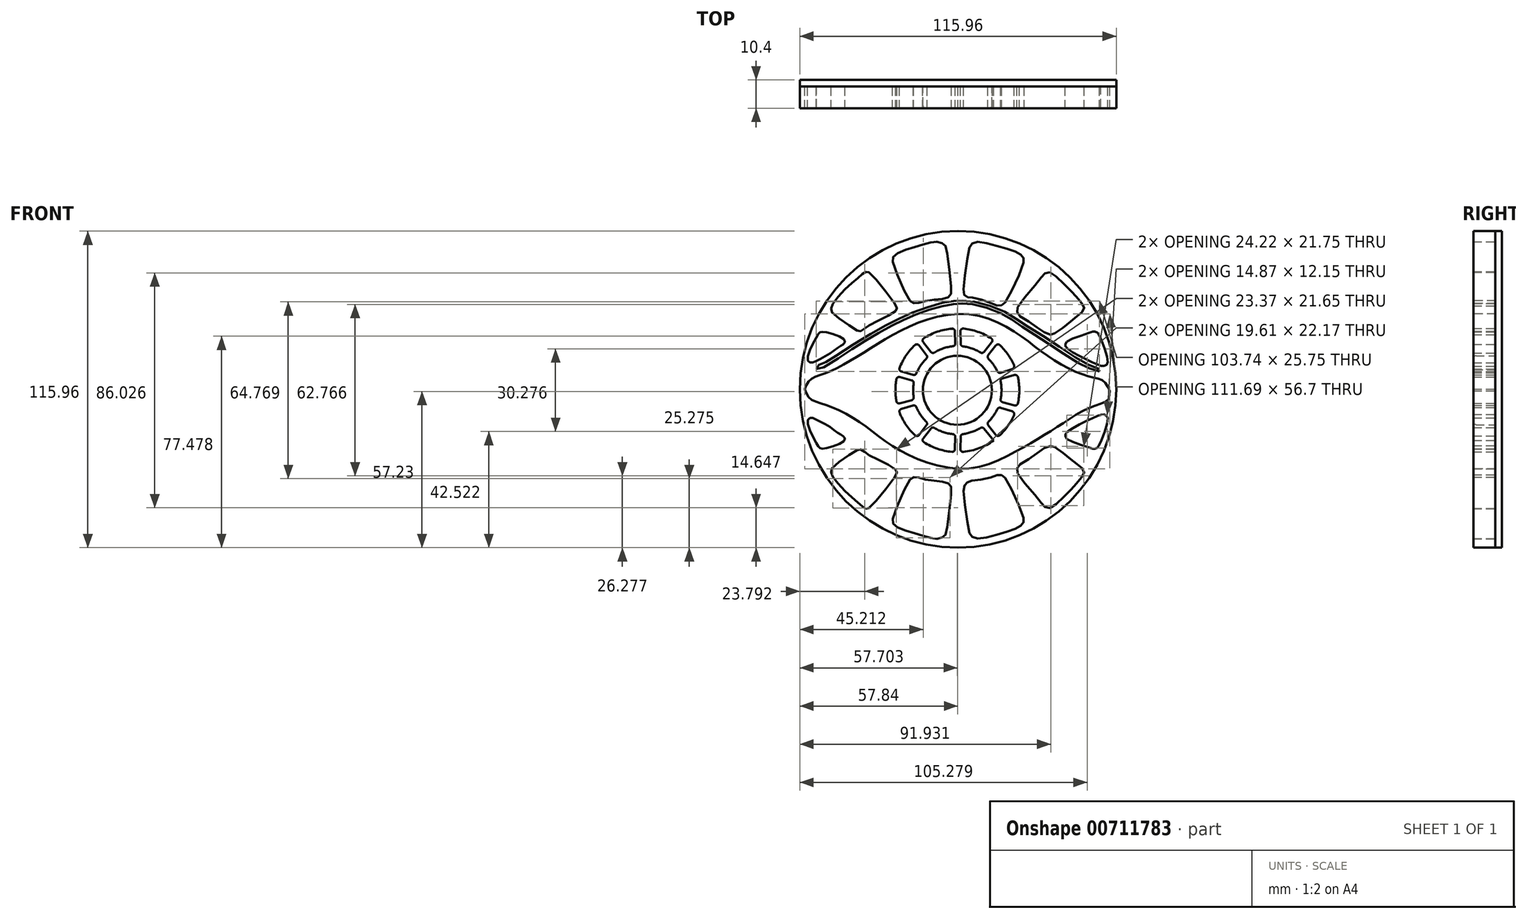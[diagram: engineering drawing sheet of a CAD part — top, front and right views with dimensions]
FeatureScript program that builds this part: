
annotation { "Feature Type Name" : "Feature", "Feature Type Description" : "" }
export const myFeature = defineFeature(function(context is Context, id is Id, definition is map)
    precondition{}
    {
        {
            var Q0;
            Q0=qCreatedBy(makeId("Front.planeOp"),FACE);
            var sketch = newSketch(context, id + "F0", { "sketchPlane" : qUnion([Q0])});
            skPoint(sketch, "E0.first.point", {"position": v(-56.19, 0) * mm});
            skPoint(sketch, "E0.second.point", {"position": v(55.8, -3.23) * mm});
            skPoint(sketch, "E0.third.point", {"position": v(-2.74, 55.09) * mm});
            skCircle(sketch, "E1", {"center": v(-0.25, -2.32) * mm, "radius": 12.63 * mm});
            skPoint(sketch, "E1.first.point", {"position": v(-12.67, 0) * mm});
            skPoint(sketch, "E1.second.point", {"position": v(12.27, -3.96) * mm});
            skPoint(sketch, "E1.third.point", {"position": v(2.35, 10.04) * mm});
            skFitSpline(sketch, "E2", {"points": [v(0, 25.6) * mm, v(22.08, 18.16) * mm, v(35.62, 8.4) * mm, v(48.16, 2.67) * mm, v(53.12, 1.17) * mm, v(55.8, -3.23) * mm], "startDerivative": vector(97.64, 3.3) * mm, "endDerivative": vector(12.94, -38.95) * mm});
            skFitSpline(sketch, "E3.MirrorCS", {"points": [v(0, 25.6) * mm, v(-22.75, 18.54) * mm, v(-38.1, 9.34) * mm, v(-48.7, 3.85) * mm, v(-54.13, 1.57) * mm, v(-56.3, -2.43) * mm], "startDerivative": vector(-92.15, -2.88) * mm, "endDerivative": vector(-12.94, -38.95) * mm});
            skFitSpline(sketch, "E4.MirrorCS", {"points": [v(0, -31.1) * mm, v(23.23, -23.62) * mm, v(36.64, -15.57) * mm, v(48.14, -8.8) * mm, v(55.17, -5.48) * mm, v(55.8, -1.41) * mm], "startDerivative": vector(97.64, -3.3) * mm, "endDerivative": vector(12.94, 38.95) * mm});
            skFitSpline(sketch, "E5.MirrorCS", {"points": [v(0, -31.1) * mm, v(-23.18, -23.24) * mm, v(-36.31, -13.78) * mm, v(-48.45, -7.65) * mm, v(-54.13, -5.41) * mm, v(-56.3, -1.41) * mm], "startDerivative": vector(-89.64, 6.19) * mm, "endDerivative": vector(-12.94, 38.95) * mm});
            skFitSpline(sketch, "E6", {"points": [v(-52, 5.4) * mm, v(-45.96, 7.88) * mm, v(-34.5, 15.43) * mm, v(-23.54, 21.65) * mm, v(-15.7, 25.25) * mm, v(-4.7, 28.68) * mm, v(0.44, 29.22) * mm], "startDerivative": vector(38.04, 9.99) * mm, "endDerivative": vector(34.79, 0.33) * mm});
            skFitSpline(sketch, "E7.MirrorCS", {"points": [v(51.82, 4.54) * mm, v(45.93, 6.75) * mm, v(33.9, 14.77) * mm, v(22.85, 21.49) * mm, v(15.76, 25.71) * mm, v(4.84, 29.15) * mm, v(-0.2, 29.2) * mm], "startDerivative": vector(-38.04, 9.99) * mm, "endDerivative": vector(-34.83, 0.37) * mm});
            skFitSpline(sketch, "E8", {"points": [v(-52.01, 8.4) * mm, v(-46.87, 11.2) * mm, v(-43.44, 13.7) * mm, v(-41.72, 14.8) * mm, v(-41.72, 16.2) * mm, v(-48.74, 19) * mm, v(-50.6, 18.84) * mm, v(-51.7, 17.29) * mm, v(-55.1, 9.31) * mm, v(-54.04, 7.78) * mm, v(-52.01, 8.4) * mm]});
            skFitSpline(sketch, "E9", {"points": [v(-45.87, 29.35) * mm, v(-40.77, 35.19) * mm, v(-36.51, 38.99) * mm, v(-34.47, 40.65) * mm, v(-33.45, 41.12) * mm, v(-32.25, 40.56) * mm, v(-22.8, 28.88) * mm, v(-22.42, 27.59) * mm, v(-23.26, 26.38) * mm, v(-31.7, 21.93) * mm, v(-34.29, 20.17) * mm, v(-35.96, 19.25) * mm, v(-37.62, 19.99) * mm, v(-45.96, 25.92) * mm, v(-46.52, 27.4) * mm, v(-45.87, 29.35) * mm]});
            skFitSpline(sketch, "E10", {"points": [v(-22.16, 47.89) * mm, v(-16.65, 49.92) * mm, v(-11.8, 51.3) * mm, v(-8.4, 52.08) * mm, v(-6.5, 51.82) * mm, v(-4.85, 50.9) * mm, v(-4.26, 49.4) * mm, v(-2.5, 34.19) * mm, v(-2.82, 32.55) * mm, v(-3.94, 31.57) * mm, v(-7.28, 30.98) * mm, v(-12.46, 30.26) * mm, v(-15.08, 29.54) * mm, v(-16.52, 29.6) * mm, v(-17.83, 30.72) * mm, v(-23.93, 44.67) * mm, v(-23.8, 46.44) * mm, v(-22.16, 47.89) * mm]});
            skFitSpline(sketch, "E11", {"points": [v(7.16, 52.01) * mm, v(14.24, 50.57) * mm, v(20.86, 48.54) * mm, v(23.28, 47.1) * mm, v(24, 46.05) * mm, v(24.07, 44.54) * mm, v(17.38, 30) * mm, v(16.07, 28.88) * mm, v(14.76, 28.62) * mm, v(11.75, 29.73) * mm, v(5.3, 31.6) * mm, v(3.6, 31.77) * mm, v(2.44, 32.42) * mm, v(2.05, 34.19) * mm, v(4.01, 49.2) * mm, v(5, 51.3) * mm, v(7.16, 52.01) * mm]});
            skFitSpline(sketch, "E12", {"points": [v(21.84, 28.1) * mm, v(29.38, 37.4) * mm, v(31.34, 40.02) * mm, v(32.78, 40.87) * mm, v(34.42, 40.48) * mm, v(39.47, 35.96) * mm, v(42.94, 32.35) * mm, v(45.37, 29.4) * mm, v(46.22, 27.83) * mm, v(45.56, 26.32) * mm, v(43.27, 24.55) * mm, v(39.53, 21.47) * mm, v(34.88, 18.2) * mm, v(33.96, 18.06) * mm, v(31.34, 19.05) * mm, v(26.69, 22.4) * mm, v(21.97, 25.4) * mm, v(21.64, 26.32) * mm, v(21.84, 28.1) * mm]});
            skFitSpline(sketch, "E13", {"points": [v(39.86, 15.5) * mm, v(48.7, 18.92) * mm, v(49.82, 19.24) * mm, v(50.87, 18.85) * mm, v(51.6, 18.13) * mm, v(54.84, 8.73) * mm, v(54.41, 6.99) * mm, v(53.17, 6.53) * mm, v(51.4, 6.99) * mm, v(44.78, 10.07) * mm, v(39.47, 13.54) * mm, v(39.27, 14.33) * mm, v(39.86, 15.5) * mm]});
            skFitSpline(sketch, "E14.MirrorC", {"points": [v(39.86, -20.15) * mm, v(48.7, -23.56) * mm, v(49.82, -23.88) * mm, v(50.87, -23.5) * mm, v(51.6, -22.77) * mm, v(54.84, -13.37) * mm, v(54.41, -11.63) * mm, v(53.17, -11.17) * mm, v(51.4, -11.63) * mm, v(44.78, -14.7) * mm, v(39.47, -18.18) * mm, v(39.27, -18.97) * mm, v(39.86, -20.15) * mm]});
            skFitSpline(sketch, "E15.MirrorC", {"points": [v(21.84, -32.73) * mm, v(29.38, -42.04) * mm, v(31.34, -44.66) * mm, v(32.78, -45.51) * mm, v(34.42, -45.12) * mm, v(39.47, -40.6) * mm, v(42.94, -37) * mm, v(45.37, -34.04) * mm, v(46.22, -32.47) * mm, v(45.56, -30.96) * mm, v(43.27, -29.2) * mm, v(39.53, -26.11) * mm, v(34.88, -22.84) * mm, v(33.96, -22.7) * mm, v(31.34, -23.69) * mm, v(26.69, -27.03) * mm, v(21.97, -30.04) * mm, v(21.64, -30.96) * mm, v(21.84, -32.73) * mm]});
            skFitSpline(sketch, "E16.MirrorC", {"points": [v(7.16, -56.65) * mm, v(14.24, -55.21) * mm, v(20.86, -53.18) * mm, v(23.28, -51.74) * mm, v(24, -50.69) * mm, v(24.07, -49.18) * mm, v(17.38, -34.63) * mm, v(16.07, -33.52) * mm, v(14.76, -33.26) * mm, v(11.75, -34.37) * mm, v(5.06, -35.48) * mm, v(3.5, -36) * mm, v(2.44, -37.06) * mm, v(2.05, -38.83) * mm, v(4.01, -53.83) * mm, v(5, -55.93) * mm, v(7.16, -56.65) * mm]});
            skFitSpline(sketch, "E17.MirrorC", {"points": [v(-22.16, -52.53) * mm, v(-16.65, -54.56) * mm, v(-11.8, -55.93) * mm, v(-8.4, -56.72) * mm, v(-6.5, -56.46) * mm, v(-4.85, -55.54) * mm, v(-4.26, -54.03) * mm, v(-2.5, -38.83) * mm, v(-2.82, -37.19) * mm, v(-3.94, -36.2) * mm, v(-7.28, -35.62) * mm, v(-12.46, -34.9) * mm, v(-15.08, -34.18) * mm, v(-16.52, -34.24) * mm, v(-17.83, -35.35) * mm, v(-23.93, -49.31) * mm, v(-23.8, -51.08) * mm, v(-22.16, -52.53) * mm]});
            skFitSpline(sketch, "E18.MirrorC", {"points": [v(-45.87, -33.99) * mm, v(-40.77, -39.83) * mm, v(-36.51, -43.63) * mm, v(-34.47, -45.3) * mm, v(-33.45, -45.76) * mm, v(-32.25, -45.2) * mm, v(-22.8, -33.52) * mm, v(-22.42, -32.23) * mm, v(-23.26, -31.02) * mm, v(-31.7, -26.57) * mm, v(-34.29, -24.81) * mm, v(-35.96, -23.89) * mm, v(-37.62, -24.63) * mm, v(-45.96, -30.56) * mm, v(-46.52, -32.04) * mm, v(-45.87, -33.99) * mm]});
            skFitSpline(sketch, "E19.MirrorC", {"points": [v(-52.01, -13.04) * mm, v(-46.87, -15.85) * mm, v(-43.44, -18.34) * mm, v(-41.72, -19.43) * mm, v(-41.72, -20.83) * mm, v(-48.74, -23.64) * mm, v(-50.6, -23.48) * mm, v(-51.7, -21.93) * mm, v(-55.1, -13.95) * mm, v(-54.04, -12.42) * mm, v(-52.01, -13.04) * mm]});
            skCircle(sketch, "E20", {"center": v(-0.25, -2.32) * mm, "radius": 58.34 * mm});
            skLineSegment(sketch, "E21.0", {"start": v(-9.43, 11) * mm, "end": v(-13.4, 16.13) * mm});
            skLineSegment(sketch, "E22.0", {"start": v(-10.98, 9.8) * mm, "end": v(-14.95, 14.97) * mm});
            skLineSegment(sketch, "E23.0", {"start": v(0.96, 13.83) * mm, "end": v(0.85, 20.35) * mm});
            skLineSegment(sketch, "E24.0", {"start": v(-0.95, 13.84) * mm, "end": v(-1.17, 20.31) * mm});
            skLineSegment(sketch, "E25.0", {"start": v(-15.55, 3.05) * mm, "end": v(-21.8, 4.82) * mm});
            skLineSegment(sketch, "E26.0", {"start": v(-16.08, 1.06) * mm, "end": v(-22.35, 2.79) * mm});
            skLineSegment(sketch, "E27.0", {"start": v(10.52, 9.8) * mm, "end": v(14.52, 14.93) * mm});
            skLineSegment(sketch, "E28.0", {"start": v(8.94, 11.01) * mm, "end": v(13.03, 16.08) * mm});
            skLineSegment(sketch, "E29.0", {"start": v(15.4, 1.82) * mm, "end": v(21.68, 3.5) * mm});
            skLineSegment(sketch, "E30.0", {"start": v(14.75, 3.82) * mm, "end": v(20.93, 5.8) * mm});
            skPoint(sketch, "E31.MirrorP", {"position": v(2.35, -14.68) * mm});
            skLineSegment(sketch, "E32.MirrorCS", {"start": v(10.52, -14.43) * mm, "end": v(14.52, -19.57) * mm});
            skLineSegment(sketch, "E33.MirrorCS", {"start": v(8.94, -15.65) * mm, "end": v(13.03, -20.72) * mm});
            skLineSegment(sketch, "E34.MirrorCS", {"start": v(-10.98, -14.44) * mm, "end": v(-14.95, -19.61) * mm});
            skLineSegment(sketch, "E35.MirrorCS", {"start": v(-9.43, -15.64) * mm, "end": v(-13.4, -20.77) * mm});
            skLineSegment(sketch, "E36.MirrorCS", {"start": v(-15.55, -7.7) * mm, "end": v(-21.8, -9.46) * mm});
            skLineSegment(sketch, "E37.MirrorCS", {"start": v(0.96, -18.47) * mm, "end": v(0.85, -24.99) * mm});
            skLineSegment(sketch, "E38.MirrorCS", {"start": v(-0.95, -18.48) * mm, "end": v(-1.17, -24.95) * mm});
            skLineSegment(sketch, "E39.MirrorCS", {"start": v(-16.08, -5.7) * mm, "end": v(-22.35, -7.43) * mm});
            skLineSegment(sketch, "E40.MirrorCS", {"start": v(15.4, -6.46) * mm, "end": v(21.68, -8.14) * mm});
            skLineSegment(sketch, "E41.MirrorCS", {"start": v(14.75, -8.46) * mm, "end": v(20.93, -10.43) * mm});
            skFitSpline(sketch, "E42.0", {"points": [v(-52.25, 6.37) * mm, v(-51.49, 6.57) * mm, v(-50.3, 6.95) * mm, v(-48.53, 7.68) * mm, v(-47.12, 8.37) * mm, v(-45.6, 9.23) * mm, v(-43.96, 10.25) * mm, v(-42.24, 11.4) * mm, v(-40.44, 12.62) * mm, v(-38.6, 13.9) * mm, v(-36.7, 15.18) * mm, v(-34.8, 16.44) * mm, v(-32.9, 17.62) * mm, v(-31.02, 18.74) * mm, v(-29.17, 19.78) * mm, v(-27.39, 20.76) * mm, v(-25.68, 21.67) * mm, v(-24.05, 22.52) * mm, v(-22.52, 23.3) * mm, v(-21.04, 24.02) * mm, v(-19.56, 24.72) * mm, v(-18.01, 25.4) * mm, v(-16.36, 26.07) * mm, v(-14.53, 26.77) * mm, v(-11.95, 27.7) * mm, v(-9.26, 28.56) * mm, v(-6.72, 29.25) * mm, v(-4.95, 29.67) * mm, v(-3.37, 29.95) * mm, v(-1.5, 30.17) * mm, v(-0.3, 30.2) * mm, v(0.44, 30.22) * mm]});
            skFitSpline(sketch, "E43.0", {"points": [v(52.07, 5.5) * mm, v(51.29, 5.71) * mm, v(50.09, 6.04) * mm, v(48.35, 6.7) * mm, v(47.19, 7.22) * mm, v(46.2, 7.74) * mm, v(45.16, 8.33) * mm, v(43.78, 9.19) * mm, v(42.02, 10.37) * mm, v(40.17, 11.65) * mm, v(38.28, 12.98) * mm, v(36.34, 14.34) * mm, v(34.39, 15.66) * mm, v(32.44, 16.9) * mm, v(30.53, 18.08) * mm, v(28.68, 19.18) * mm, v(26.9, 20.22) * mm, v(25.23, 21.2) * mm, v(23.68, 22.14) * mm, v(22.27, 23.04) * mm, v(20.92, 23.91) * mm, v(19.57, 24.77) * mm, v(18.15, 25.61) * mm, v(16.58, 26.44) * mm, v(14.81, 27.26) * mm, v(12.88, 28.03) * mm, v(10.88, 28.74) * mm, v(8.87, 29.34) * mm, v(7.24, 29.75) * mm, v(6, 30) * mm, v(5.12, 30.13) * mm, v(4.28, 30.22) * mm, v(3.23, 30.29) * mm, v(2.06, 30.28) * mm, v(0.84, 30.23) * mm, v(0.14, 30.2) * mm, v(-0.2, 30.2) * mm]});
            skLineSegment(sketch, "E44", {"start": v(-0.2, 29.2) * mm, "end": v(0.44, 29.22) * mm});
            skLineSegment(sketch, "E45", {"start": v(-52.25, 6.37) * mm, "end": v(-52, 5.4) * mm});
            skLineSegment(sketch, "E46", {"start": v(51.96, 5.53) * mm, "end": v(51.82, 4.54) * mm});
            skArc(sketch, "E47", {"start": v(-9.43, 11) * mm, "mid": v(-5.39, 13.01) * mm, "end": v(-0.95, 13.84) * mm});
            skArc(sketch, "E48", {"start": v(0.96, 13.83) * mm, "mid": v(5.14, 12.95) * mm, "end": v(8.94, 11.01) * mm});
            skArc(sketch, "E49", {"start": v(10.52, 9.8) * mm, "mid": v(12.98, 7.05) * mm, "end": v(14.75, 3.82) * mm});
            skArc(sketch, "E50", {"start": v(-15.55, 3.05) * mm, "mid": v(-13.71, 6.73) * mm, "end": v(-11, 9.82) * mm});
            skArc(sketch, "E51", {"start": v(-16.08, -5.7) * mm, "mid": v(-16.43, -2.32) * mm, "end": v(-16.08, 1.06) * mm});
            skArc(sketch, "E52", {"start": v(-15.55, -7.7) * mm, "mid": v(-13.71, -11.37) * mm, "end": v(-11, -14.46) * mm});
            skArc(sketch, "E53", {"start": v(-9.43, -15.64) * mm, "mid": v(-5.39, -17.65) * mm, "end": v(-0.95, -18.48) * mm});
            skArc(sketch, "E54", {"start": v(0.96, -18.47) * mm, "mid": v(5.14, -17.6) * mm, "end": v(8.94, -15.65) * mm});
            skArc(sketch, "E55", {"start": v(10.52, -14.43) * mm, "mid": v(12.98, -11.69) * mm, "end": v(14.75, -8.46) * mm});
            skArc(sketch, "E56", {"start": v(15.4, -6.46) * mm, "mid": v(15.93, -2.32) * mm, "end": v(15.4, 1.82) * mm});
            skArc(sketch, "E57", {"start": v(-13.4, 16.13) * mm, "mid": v(-7.59, 19.11) * mm, "end": v(-1.17, 20.31) * mm});
            skArc(sketch, "E58", {"start": v(0.85, 20.35) * mm, "mid": v(7.25, 19.1) * mm, "end": v(13.03, 16.08) * mm});
            skArc(sketch, "E59", {"start": v(-21.8, 4.82) * mm, "mid": v(-19.07, 10.37) * mm, "end": v(-14.95, 14.97) * mm});
            skArc(sketch, "E60", {"start": v(-22.35, -7.43) * mm, "mid": v(-22.93, -2.32) * mm, "end": v(-22.35, 2.79) * mm});
            skArc(sketch, "E61", {"start": v(-21.8, -9.46) * mm, "mid": v(-19.05, -15) * mm, "end": v(-14.92, -19.58) * mm});
            skArc(sketch, "E62", {"start": v(14.52, 14.93) * mm, "mid": v(18.3, 10.76) * mm, "end": v(20.92, 5.79) * mm});
            skArc(sketch, "E63", {"start": v(21.68, 3.5) * mm, "mid": v(22.44, -2.32) * mm, "end": v(21.68, -8.14) * mm});
            skArc(sketch, "E64", {"start": v(20.93, -10.43) * mm, "mid": v(18.27, -15.37) * mm, "end": v(14.47, -19.5) * mm});
            skArc(sketch, "E65", {"start": v(13.03, -20.72) * mm, "mid": v(7.25, -23.74) * mm, "end": v(0.85, -24.99) * mm});
            skArc(sketch, "E66", {"start": v(-1.17, -24.95) * mm, "mid": v(-7.59, -23.75) * mm, "end": v(-13.4, -20.77) * mm});
            skSolve(sketch);
        }
        {
            var Q0;
            Q0=qCreatedBy(makeId("Front.planeOp"),FACE);
            var sketch = newSketch(context, id + "F1", { "sketchPlane" : qUnion([Q0])});
            skCircle(sketch, "E67", {"center": v(0, -2) * mm, "radius": 57.98 * mm});
            skSolve(sketch);
        }
        {
            var Q0;
            Q0=qSketchRegion(id+"F1",true);
            extrude(context, id + "F2", {"entities" : qUnion([Q0]), "depth" : 8 * mm, "offsetDistance" : 25 * mm});
        }
        {
            var Q0;
            Q0=qSketchRegion(id+"F1",true);
            extrude(context, id + "F3", {"entities" : qUnion([Q0]), "oppositeDirection" : true, "depth" : 2.4 * mm, "offsetDistance" : 25 * mm});
        }
        {
            var Q0;
            Q0=makeQuery(id+"F0.imprint","IMPRINT",FACE,{"disambiguationData":[TD([[makeQuery(id+"F0.imprint","IMPRINT",EDGE,{"derivedFrom":sQuery(id+"F0.wireOp",EDGE,"E9")}),-1.0]])]});
            var Q1;
            Q1=makeQuery(id+"F0.imprint","IMPRINT",FACE,{"disambiguationData":[TD([[makeQuery(id+"F0.imprint","IMPRINT",EDGE,{"derivedFrom":sQuery(id+"F0.wireOp",EDGE,"E10")}),-1.0]])]});
            var Q2;
            Q2=makeQuery(id+"F0.imprint","IMPRINT",FACE,{"disambiguationData":[TD([[makeQuery(id+"F0.imprint","IMPRINT",EDGE,{"derivedFrom":sQuery(id+"F0.wireOp",EDGE,"E11")}),-1.0]])]});
            var Q3;
            Q3=makeQuery(id+"F0.imprint","IMPRINT",FACE,{"disambiguationData":[TD([[makeQuery(id+"F0.imprint","IMPRINT",EDGE,{"derivedFrom":sQuery(id+"F0.wireOp",EDGE,"E12")}),-1.0]])]});
            var Q4;
            {var subQ7=sQuery(id+"F0.wireOp",EDGE,"E3.MirrorCS");var subQ8=sQuery(id+"F0.wireOp",EDGE,"E2");var subQ9=makeQuery(id+"F0.imprint","INTERSECT",VERTEX,{"derivedFrom":[subQ8,subQ7]});Q4=makeQuery(id+"F0.imprint","IMPRINT",FACE,{"disambiguationData":[TD([[makeQuery(id+"F0.imprint","IMPRINT",EDGE,{"disambiguationData":[TD([[subQ9,-1.0]])],"derivedFrom":subQ8}),-1.0]])]});}
            var Q5;
            {var subQ4=sQuery(id+"F0.wireOp",EDGE,"E22.0");Q5=makeQuery(id+"F0.imprint","IMPRINT",FACE,{"disambiguationData":[TD([[makeQuery(id+"F0.imprint","IMPRINT",EDGE,{"derivedFrom":subQ4}),-1.0]])]});}
            var Q6;
            {var subQ0=sQuery(id+"F0.wireOp",EDGE,"E23.0");Q6=makeQuery(id+"F0.imprint","IMPRINT",FACE,{"disambiguationData":[TD([[makeQuery(id+"F0.imprint","IMPRINT",EDGE,{"derivedFrom":subQ0}),1.0]])]});}
            var Q7;
            {var subQ1=sQuery(id+"F0.wireOp",EDGE,"E27.0");Q7=makeQuery(id+"F0.imprint","IMPRINT",FACE,{"disambiguationData":[TD([[makeQuery(id+"F0.imprint","IMPRINT",EDGE,{"derivedFrom":subQ1}),1.0]])]});}
            var Q8;
            {var subQ2=sQuery(id+"F0.wireOp",EDGE,"E29.0");Q8=makeQuery(id+"F0.imprint","IMPRINT",FACE,{"disambiguationData":[TD([[makeQuery(id+"F0.imprint","IMPRINT",EDGE,{"derivedFrom":subQ2}),1.0]])]});}
            var Q9;
            {var subQ4=sQuery(id+"F0.wireOp",EDGE,"E40.MirrorCS");Q9=makeQuery(id+"F0.imprint","IMPRINT",FACE,{"disambiguationData":[TD([[makeQuery(id+"F0.imprint","IMPRINT",EDGE,{"derivedFrom":subQ4}),-1.0]])]});}
            var Q10;
            Q10=makeQuery(id+"F0.imprint","IMPRINT",FACE,{"disambiguationData":[TD([[makeQuery(id+"F0.imprint","IMPRINT",EDGE,{"derivedFrom":sQuery(id+"F0.wireOp",EDGE,"fab38fe7-764f-41c1-85e6-31b15052e3932.MirrorCS")}),1.0]])]});
            var Q11;
            Q11=makeQuery(id+"F0.imprint","IMPRINT",FACE,{"disambiguationData":[TD([[makeQuery(id+"F0.imprint","IMPRINT",EDGE,{"derivedFrom":sQuery(id+"F0.wireOp",EDGE,"fab38fe7-764f-41c1-85e6-31b15052e3934.MirrorCS")}),1.0]])]});
            var Q12;
            {var subQ0=sQuery(id+"F0.wireOp",EDGE,"fab38fe7-764f-41c1-85e6-31b15052e3930.MirrorCS");Q12=makeQuery(id+"F0.imprint","IMPRINT",FACE,{"disambiguationData":[TD([[makeQuery(id+"F0.imprint","IMPRINT",EDGE,{"derivedFrom":subQ0}),1.0]])]});}
            var Q13;
            Q13=makeQuery(id+"F0.imprint","IMPRINT",FACE,{"disambiguationData":[TD([[makeQuery(id+"F0.imprint","IMPRINT",EDGE,{"derivedFrom":sQuery(id+"F0.wireOp",EDGE,"fab38fe7-764f-41c1-85e6-31b15052e3936.MirrorCS")}),1.0]])]});
            var Q14;
            {var subQ1=sQuery(id+"F0.wireOp",EDGE,"E25.0");Q14=makeQuery(id+"F0.imprint","IMPRINT",FACE,{"disambiguationData":[TD([[makeQuery(id+"F0.imprint","IMPRINT",EDGE,{"derivedFrom":subQ1}),1.0]])]});}
            var Q15;
            Q15=makeQuery(id+"F0.imprint","IMPRINT",FACE,{"disambiguationData":[TD([[makeQuery(id+"F0.imprint","IMPRINT",EDGE,{"derivedFrom":sQuery(id+"F0.wireOp",EDGE,"E1")}),-1.0]])]});
            var Q16;
            Q16=makeQuery(id+"F0.imprint","IMPRINT",FACE,{"disambiguationData":[TD([[makeQuery(id+"F0.imprint","IMPRINT",EDGE,{"derivedFrom":sQuery(id+"F0.wireOp",EDGE,"E8")}),1.0]])]});
            var Q17;
            Q17=makeQuery(id+"F0.imprint","IMPRINT",FACE,{"disambiguationData":[TD([[makeQuery(id+"F0.imprint","IMPRINT",EDGE,{"derivedFrom":sQuery(id+"F0.wireOp",EDGE,"E13")}),-1.0]])]});
            var Q18;
            Q18=makeQuery(id+"F0.imprint","IMPRINT",FACE,{"disambiguationData":[TD([[makeQuery(id+"F0.imprint","IMPRINT",EDGE,{"derivedFrom":sQuery(id+"F0.wireOp",EDGE,"E14.MirrorC")}),1.0]])]});
            var Q19;
            Q19=makeQuery(id+"F0.imprint","IMPRINT",FACE,{"disambiguationData":[TD([[makeQuery(id+"F0.imprint","IMPRINT",EDGE,{"derivedFrom":sQuery(id+"F0.wireOp",EDGE,"E15.MirrorC")}),1.0]])]});
            var Q20;
            Q20=makeQuery(id+"F0.imprint","IMPRINT",FACE,{"disambiguationData":[TD([[makeQuery(id+"F0.imprint","IMPRINT",EDGE,{"derivedFrom":sQuery(id+"F0.wireOp",EDGE,"E16.MirrorC")}),1.0]])]});
            var Q21;
            Q21=makeQuery(id+"F0.imprint","IMPRINT",FACE,{"disambiguationData":[TD([[makeQuery(id+"F0.imprint","IMPRINT",EDGE,{"derivedFrom":sQuery(id+"F0.wireOp",EDGE,"E17.MirrorC")}),1.0]])]});
            var Q22;
            Q22=makeQuery(id+"F0.imprint","IMPRINT",FACE,{"disambiguationData":[TD([[makeQuery(id+"F0.imprint","IMPRINT",EDGE,{"derivedFrom":sQuery(id+"F0.wireOp",EDGE,"E18.MirrorC")}),1.0]])]});
            var Q23;
            Q23=makeQuery(id+"F0.imprint","IMPRINT",FACE,{"disambiguationData":[TD([[makeQuery(id+"F0.imprint","IMPRINT",EDGE,{"derivedFrom":sQuery(id+"F0.wireOp",EDGE,"E19.MirrorC")}),-1.0]])]});
            extrude(context, id + "F4", {"entities" : qUnion([Q0, Q1, Q2, Q3, Q4, Q5, Q6, Q7, Q8, Q9, Q10, Q11, Q12, Q13, Q14, Q15, Q16, Q17, Q18, Q19, Q20, Q21, Q22, Q23]), "operationType" : NewBodyOperationType.REMOVE, "depth" : 54 * mm, "offsetDistance" : 25 * mm});
        }
        {
            var Q0;
            Q0=qCreatedBy(makeId("Front.planeOp"),FACE);
            var sketch = newSketch(context, id + "F5", { "sketchPlane" : qUnion([Q0])});
            skFitSpline(sketch, "E68", {"points": [v(51.73, 4.62) * mm, v(45.97, 6.68) * mm, v(33.43, 14.5) * mm, v(22.66, 21.52) * mm, v(15.59, 25.92) * mm, v(4.74, 29.24) * mm, v(0, 29.34) * mm, v(-5.9, 28.46) * mm, v(-15.38, 25.43) * mm, v(-23.69, 21.62) * mm, v(-34.34, 15.57) * mm, v(-45.96, 8.04) * mm, v(-52.01, 5.48) * mm], "startDerivative": vector(-81.76, 20.23) * mm, "endDerivative": vector(1.8, 51.56) * mm});
            skFitSpline(sketch, "E69", {"points": [v(-52.01, 5.48) * mm, v(-52.01, 6.3) * mm, v(-49.46, 7.46) * mm, v(-47.8, 8.36) * mm, v(-34.8, 16.66) * mm, v(-23.3, 23.06) * mm, v(-14.34, 27) * mm, v(-4.24, 29.96) * mm, v(0, 30.37) * mm, v(4.88, 30.21) * mm, v(15.97, 26.92) * mm, v(22.66, 22.8) * mm, v(34.12, 15.67) * mm, v(46.45, 7.7) * mm, v(51.54, 5.48) * mm, v(52.15, 4.94) * mm, v(51.73, 4.62) * mm], "startDerivative": vector(-11.3, 39.4) * mm, "endDerivative": vector(-33.35, -16.31) * mm});
            skSolve(sketch);
        }
        {
            var Q0;
            Q0=qSketchRegion(id+"F5",true);
            extrude(context, id + "F6", {"entities" : qUnion([Q0]), "operationType" : NewBodyOperationType.REMOVE, "depth" : 55 * mm, "offsetDistance" : 25 * mm});
        }
        {
            var Q0;
            Q0=makeQuery(id+"F4.boolean.opBoolean","COPY",EDGE,{"derivedFrom":makeQuery(id+"F4.opExtrude","SWEPT_EDGE",EDGE,{"disambiguationData":[OSD([sQuery(id+"F0.wireOp",EDGE,"E24.0"),sQuery(id+"F0.wireOp",EDGE,"E57")])]})});
            var Q1;
            Q1=makeQuery(id+"F4.boolean.opBoolean","COPY",EDGE,{"derivedFrom":makeQuery(id+"F4.opExtrude","SWEPT_EDGE",EDGE,{"disambiguationData":[OSD([sQuery(id+"F0.wireOp",EDGE,"E24.0"),sQuery(id+"F0.wireOp",EDGE,"E47")])]})});
            var Q2;
            Q2=makeQuery(id+"F4.boolean.opBoolean","COPY",EDGE,{"derivedFrom":makeQuery(id+"F4.opExtrude","SWEPT_EDGE",EDGE,{"disambiguationData":[OSD([sQuery(id+"F0.wireOp",EDGE,"E21.0"),sQuery(id+"F0.wireOp",EDGE,"E47")])]})});
            var Q3;
            Q3=makeQuery(id+"F4.boolean.opBoolean","COPY",EDGE,{"derivedFrom":makeQuery(id+"F4.opExtrude","SWEPT_EDGE",EDGE,{"disambiguationData":[OSD([sQuery(id+"F0.wireOp",EDGE,"E21.0"),sQuery(id+"F0.wireOp",EDGE,"E57")])]})});
            var Q4;
            Q4=makeQuery(id+"F4.boolean.opBoolean","COPY",EDGE,{"derivedFrom":makeQuery(id+"F4.opExtrude","SWEPT_EDGE",EDGE,{"disambiguationData":[OSD([sQuery(id+"F0.wireOp",EDGE,"E22.0"),sQuery(id+"F0.wireOp",EDGE,"E50")])]})});
            var Q5;
            Q5=makeQuery(id+"F4.boolean.opBoolean","COPY",EDGE,{"derivedFrom":makeQuery(id+"F4.opExtrude","SWEPT_EDGE",EDGE,{"disambiguationData":[OSD([sQuery(id+"F0.wireOp",EDGE,"E22.0"),sQuery(id+"F0.wireOp",EDGE,"E59")])]})});
            var Q6;
            Q6=makeQuery(id+"F4.boolean.opBoolean","COPY",EDGE,{"derivedFrom":makeQuery(id+"F4.opExtrude","SWEPT_EDGE",EDGE,{"disambiguationData":[OSD([sQuery(id+"F0.wireOp",EDGE,"E26.0"),sQuery(id+"F0.wireOp",EDGE,"E51")])]})});
            var Q7;
            Q7=makeQuery(id+"F4.boolean.opBoolean","COPY",EDGE,{"derivedFrom":makeQuery(id+"F4.opExtrude","SWEPT_EDGE",EDGE,{"disambiguationData":[OSD([sQuery(id+"F0.wireOp",EDGE,"E26.0"),sQuery(id+"F0.wireOp",EDGE,"E60")])]})});
            var Q8;
            Q8=makeQuery(id+"F4.boolean.opBoolean","COPY",EDGE,{"derivedFrom":makeQuery(id+"F4.opExtrude","SWEPT_EDGE",EDGE,{"disambiguationData":[OSD([sQuery(id+"F0.wireOp",EDGE,"E25.0"),sQuery(id+"F0.wireOp",EDGE,"E59")])]})});
            var Q9;
            Q9=makeQuery(id+"F4.boolean.opBoolean","COPY",EDGE,{"derivedFrom":makeQuery(id+"F4.opExtrude","SWEPT_EDGE",EDGE,{"disambiguationData":[OSD([sQuery(id+"F0.wireOp",EDGE,"E39.MirrorCS"),sQuery(id+"F0.wireOp",EDGE,"E60")])]})});
            var Q10;
            Q10=makeQuery(id+"F4.boolean.opBoolean","COPY",EDGE,{"derivedFrom":makeQuery(id+"F4.opExtrude","SWEPT_EDGE",EDGE,{"disambiguationData":[OSD([sQuery(id+"F0.wireOp",EDGE,"E39.MirrorCS"),sQuery(id+"F0.wireOp",EDGE,"E51")])]})});
            var Q11;
            Q11=makeQuery(id+"F4.boolean.opBoolean","COPY",EDGE,{"derivedFrom":makeQuery(id+"F4.opExtrude","SWEPT_EDGE",EDGE,{"disambiguationData":[OSD([sQuery(id+"F0.wireOp",EDGE,"E36.MirrorCS"),sQuery(id+"F0.wireOp",EDGE,"E61")])]})});
            var Q12;
            Q12=makeQuery(id+"F4.boolean.opBoolean","COPY",EDGE,{"derivedFrom":makeQuery(id+"F4.opExtrude","SWEPT_EDGE",EDGE,{"disambiguationData":[OSD([sQuery(id+"F0.wireOp",EDGE,"E34.MirrorCS"),sQuery(id+"F0.wireOp",EDGE,"E61")])]})});
            var Q13;
            Q13=makeQuery(id+"F4.boolean.opBoolean","COPY",EDGE,{"derivedFrom":makeQuery(id+"F4.opExtrude","SWEPT_EDGE",EDGE,{"disambiguationData":[OSD([sQuery(id+"F0.wireOp",EDGE,"E35.MirrorCS"),sQuery(id+"F0.wireOp",EDGE,"E66")])]})});
            var Q14;
            Q14=makeQuery(id+"F4.boolean.opBoolean","COPY",EDGE,{"derivedFrom":makeQuery(id+"F4.opExtrude","SWEPT_EDGE",EDGE,{"disambiguationData":[OSD([sQuery(id+"F0.wireOp",EDGE,"E38.MirrorCS"),sQuery(id+"F0.wireOp",EDGE,"E66")])]})});
            var Q15;
            Q15=makeQuery(id+"F4.boolean.opBoolean","COPY",EDGE,{"derivedFrom":makeQuery(id+"F4.opExtrude","SWEPT_EDGE",EDGE,{"disambiguationData":[OSD([sQuery(id+"F0.wireOp",EDGE,"E37.MirrorCS"),sQuery(id+"F0.wireOp",EDGE,"E65")])]})});
            var Q16;
            Q16=makeQuery(id+"F4.boolean.opBoolean","COPY",EDGE,{"derivedFrom":makeQuery(id+"F4.opExtrude","SWEPT_EDGE",EDGE,{"disambiguationData":[OSD([sQuery(id+"F0.wireOp",EDGE,"E32.MirrorCS"),sQuery(id+"F0.wireOp",EDGE,"E64")])]})});
            var Q17;
            Q17=makeQuery(id+"F4.boolean.opBoolean","COPY",EDGE,{"derivedFrom":makeQuery(id+"F4.opExtrude","SWEPT_EDGE",EDGE,{"disambiguationData":[OSD([sQuery(id+"F0.wireOp",EDGE,"E32.MirrorCS"),sQuery(id+"F0.wireOp",EDGE,"E55")])]})});
            var Q18;
            Q18=makeQuery(id+"F4.boolean.opBoolean","COPY",EDGE,{"derivedFrom":makeQuery(id+"F4.opExtrude","SWEPT_EDGE",EDGE,{"disambiguationData":[OSD([sQuery(id+"F0.wireOp",EDGE,"E40.MirrorCS"),sQuery(id+"F0.wireOp",EDGE,"E56")])]})});
            var Q19;
            Q19=makeQuery(id+"F4.boolean.opBoolean","COPY",EDGE,{"derivedFrom":makeQuery(id+"F4.opExtrude","SWEPT_EDGE",EDGE,{"disambiguationData":[OSD([sQuery(id+"F0.wireOp",EDGE,"E41.MirrorCS"),sQuery(id+"F0.wireOp",EDGE,"E55")])]})});
            var Q20;
            Q20=makeQuery(id+"F4.boolean.opBoolean","COPY",EDGE,{"derivedFrom":makeQuery(id+"F4.opExtrude","SWEPT_EDGE",EDGE,{"disambiguationData":[OSD([sQuery(id+"F0.wireOp",EDGE,"E40.MirrorCS"),sQuery(id+"F0.wireOp",EDGE,"E63")])]})});
            var Q21;
            Q21=makeQuery(id+"F4.boolean.opBoolean","COPY",EDGE,{"derivedFrom":makeQuery(id+"F4.opExtrude","SWEPT_EDGE",EDGE,{"disambiguationData":[OSD([sQuery(id+"F0.wireOp",EDGE,"E29.0"),sQuery(id+"F0.wireOp",EDGE,"E56")])]})});
            var Q22;
            Q22=makeQuery(id+"F4.boolean.opBoolean","COPY",EDGE,{"derivedFrom":makeQuery(id+"F4.opExtrude","SWEPT_EDGE",EDGE,{"disambiguationData":[OSD([sQuery(id+"F0.wireOp",EDGE,"E30.0"),sQuery(id+"F0.wireOp",EDGE,"E49")])]})});
            var Q23;
            Q23=makeQuery(id+"F4.boolean.opBoolean","COPY",EDGE,{"derivedFrom":makeQuery(id+"F4.opExtrude","SWEPT_EDGE",EDGE,{"disambiguationData":[OSD([sQuery(id+"F0.wireOp",EDGE,"E27.0"),sQuery(id+"F0.wireOp",EDGE,"E49")])]})});
            var Q24;
            Q24=makeQuery(id+"F4.boolean.opBoolean","COPY",EDGE,{"derivedFrom":makeQuery(id+"F4.opExtrude","SWEPT_EDGE",EDGE,{"disambiguationData":[OSD([sQuery(id+"F0.wireOp",EDGE,"E28.0"),sQuery(id+"F0.wireOp",EDGE,"E48")])]})});
            var Q25;
            Q25=makeQuery(id+"F4.boolean.opBoolean","COPY",EDGE,{"derivedFrom":makeQuery(id+"F4.opExtrude","SWEPT_EDGE",EDGE,{"disambiguationData":[OSD([sQuery(id+"F0.wireOp",EDGE,"E23.0"),sQuery(id+"F0.wireOp",EDGE,"E48")])]})});
            var Q26;
            Q26=makeQuery(id+"F4.boolean.opBoolean","COPY",EDGE,{"derivedFrom":makeQuery(id+"F4.opExtrude","SWEPT_EDGE",EDGE,{"disambiguationData":[OSD([sQuery(id+"F0.wireOp",EDGE,"E25.0"),sQuery(id+"F0.wireOp",EDGE,"E50")])]})});
            var Q27;
            Q27=makeQuery(id+"F4.boolean.opBoolean","COPY",EDGE,{"derivedFrom":makeQuery(id+"F4.opExtrude","SWEPT_EDGE",EDGE,{"disambiguationData":[OSD([sQuery(id+"F0.wireOp",EDGE,"E30.0"),sQuery(id+"F0.wireOp",EDGE,"E62")])]})});
            var Q28;
            Q28=makeQuery(id+"F4.boolean.opBoolean","COPY",EDGE,{"derivedFrom":makeQuery(id+"F4.opExtrude","SWEPT_EDGE",EDGE,{"disambiguationData":[OSD([sQuery(id+"F0.wireOp",EDGE,"E27.0"),sQuery(id+"F0.wireOp",EDGE,"E62")])]})});
            var Q29;
            Q29=makeQuery(id+"F4.boolean.opBoolean","COPY",EDGE,{"derivedFrom":makeQuery(id+"F4.opExtrude","SWEPT_EDGE",EDGE,{"disambiguationData":[OSD([sQuery(id+"F0.wireOp",EDGE,"E38.MirrorCS"),sQuery(id+"F0.wireOp",EDGE,"E53")])]})});
            var Q30;
            Q30=makeQuery(id+"F4.boolean.opBoolean","COPY",EDGE,{"derivedFrom":makeQuery(id+"F4.opExtrude","SWEPT_EDGE",EDGE,{"disambiguationData":[OSD([sQuery(id+"F0.wireOp",EDGE,"E35.MirrorCS"),sQuery(id+"F0.wireOp",EDGE,"E53")])]})});
            var Q31;
            Q31=makeQuery(id+"F4.boolean.opBoolean","COPY",EDGE,{"derivedFrom":makeQuery(id+"F4.opExtrude","SWEPT_EDGE",EDGE,{"disambiguationData":[OSD([sQuery(id+"F0.wireOp",EDGE,"E34.MirrorCS"),sQuery(id+"F0.wireOp",EDGE,"E52")])]})});
            var Q32;
            Q32=makeQuery(id+"F4.boolean.opBoolean","COPY",EDGE,{"derivedFrom":makeQuery(id+"F4.opExtrude","SWEPT_EDGE",EDGE,{"disambiguationData":[OSD([sQuery(id+"F0.wireOp",EDGE,"E36.MirrorCS"),sQuery(id+"F0.wireOp",EDGE,"E52")])]})});
            var Q33;
            Q33=makeQuery(id+"F4.boolean.opBoolean","COPY",EDGE,{"derivedFrom":makeQuery(id+"F4.opExtrude","SWEPT_EDGE",EDGE,{"disambiguationData":[OSD([sQuery(id+"F0.wireOp",EDGE,"E29.0"),sQuery(id+"F0.wireOp",EDGE,"E63")])]})});
            var Q34;
            Q34=makeQuery(id+"F4.boolean.opBoolean","COPY",EDGE,{"derivedFrom":makeQuery(id+"F4.opExtrude","SWEPT_EDGE",EDGE,{"disambiguationData":[OSD([sQuery(id+"F0.wireOp",EDGE,"E41.MirrorCS"),sQuery(id+"F0.wireOp",EDGE,"E64")])]})});
            var Q35;
            Q35=makeQuery(id+"F4.boolean.opBoolean","COPY",EDGE,{"derivedFrom":makeQuery(id+"F4.opExtrude","SWEPT_EDGE",EDGE,{"disambiguationData":[OSD([sQuery(id+"F0.wireOp",EDGE,"E23.0"),sQuery(id+"F0.wireOp",EDGE,"E58")])]})});
            var Q36;
            Q36=makeQuery(id+"F4.boolean.opBoolean","COPY",EDGE,{"derivedFrom":makeQuery(id+"F4.opExtrude","SWEPT_EDGE",EDGE,{"disambiguationData":[OSD([sQuery(id+"F0.wireOp",EDGE,"E28.0"),sQuery(id+"F0.wireOp",EDGE,"E58")])]})});
            var Q37;
            Q37=makeQuery(id+"F4.boolean.opBoolean","COPY",EDGE,{"derivedFrom":makeQuery(id+"F4.opExtrude","SWEPT_EDGE",EDGE,{"disambiguationData":[OSD([sQuery(id+"F0.wireOp",EDGE,"E37.MirrorCS"),sQuery(id+"F0.wireOp",EDGE,"E54")])]})});
            var Q38;
            Q38=makeQuery(id+"F4.boolean.opBoolean","COPY",EDGE,{"derivedFrom":makeQuery(id+"F4.opExtrude","SWEPT_EDGE",EDGE,{"disambiguationData":[OSD([sQuery(id+"F0.wireOp",EDGE,"E33.MirrorCS"),sQuery(id+"F0.wireOp",EDGE,"E54")])]})});
            var Q39;
            Q39=makeQuery(id+"F4.boolean.opBoolean","INTERSECT",EDGE,{"derivedFrom":[makeQuery(id+"F2.opExtrude","CAP_FACE",FACE,{"disambiguationData":[OSD([sQuery(id+"F1.wireOp",EDGE,"E67")])],"isStart":false}),makeQuery(id+"F4.opExtrude","SWEPT_FACE",FACE,{"disambiguationData":[OSD([sQuery(id+"F0.wireOp",EDGE,"E1")])]})]});
            fillet(context, id + "F7", {"entities" : qUnion([Q0, Q1, Q2, Q3, Q4, Q5, Q6, Q7, Q8, Q9, Q10, Q11, Q12, Q13, Q14, Q15, Q16, Q17, Q18, Q19, Q20, Q21, Q22, Q23, Q24, Q25, Q26, Q27, Q28, Q29, Q30, Q31, Q32, Q33, Q34, Q35, Q36, Q37, Q38, Q39]), "radius" : 1 * mm, "tangentPropagation" : true, "allowEdgeOverflow" : false});
        }
    });
